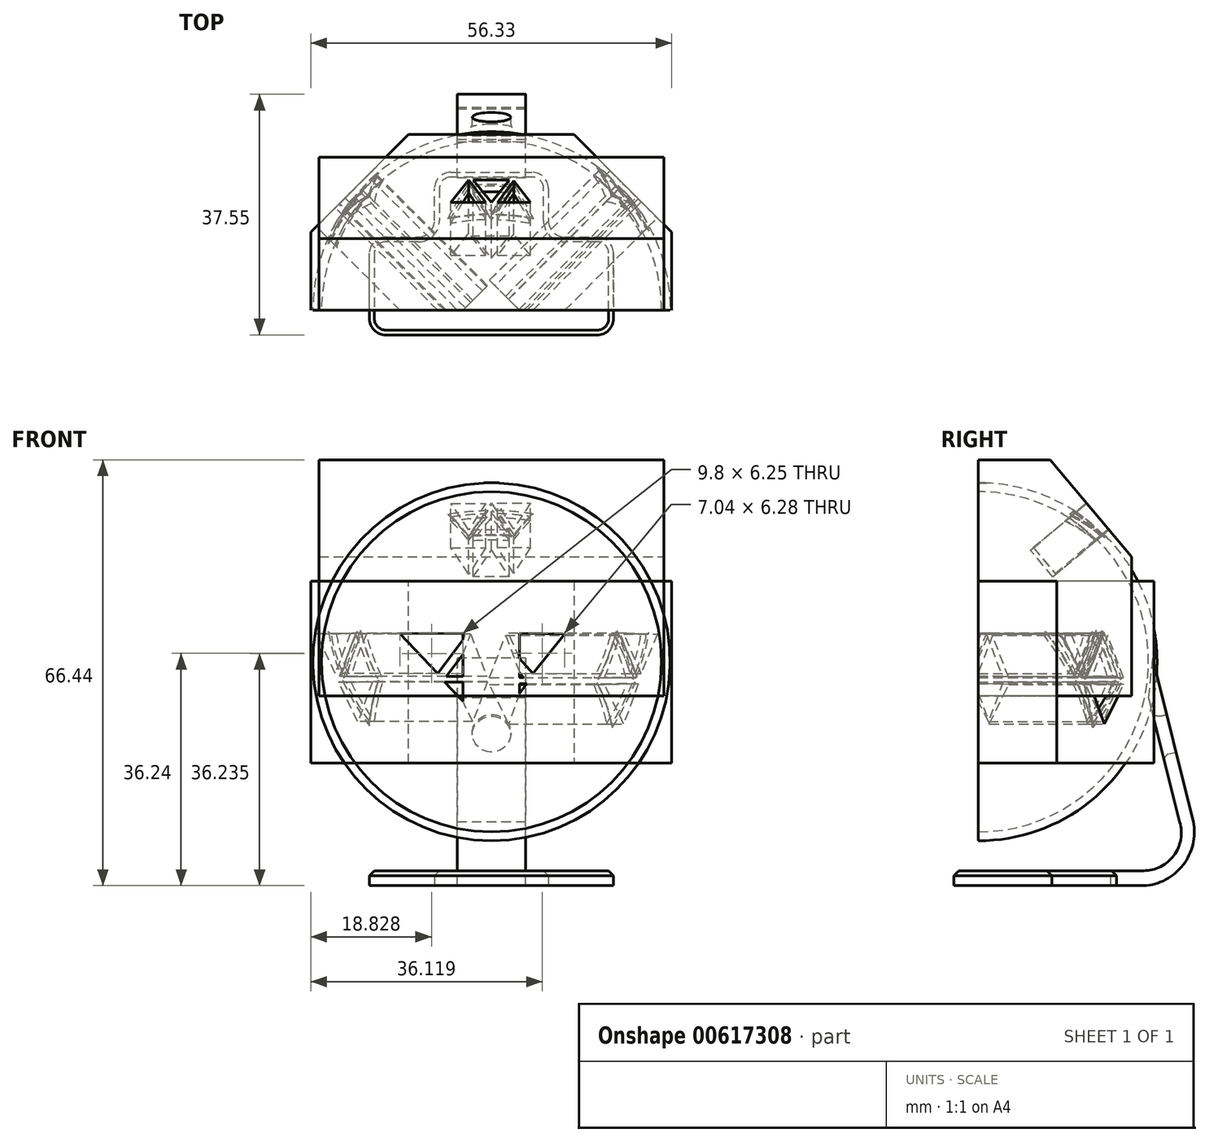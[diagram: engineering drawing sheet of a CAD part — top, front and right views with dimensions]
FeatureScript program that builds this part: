
annotation { "Feature Type Name" : "Feature", "Feature Type Description" : "" }
export const myFeature = defineFeature(function(context is Context, id is Id, definition is map)
    precondition{}
    {
        {
            var Q0;
            Q0=qCreatedBy(makeId("Front.planeOp"),FACE);
            var sketch = newSketch(context, id + "F0", { "sketchPlane" : qUnion([Q0])});
            skLineSegment(sketch, "E0", {"start": v(0, 76.83) * mm, "end": v(0, 0) * mm, "construction": true});
            skCircle(sketch, "E1", {"center": v(0, 34.92) * mm, "radius": 26.54 * mm});
            skCircle(sketch, "E2", {"center": v(0, 34.92) * mm, "radius": 27.94 * mm});
            skSolve(sketch);
        }
        {
            var Q0;
            Q0=makeQuery(id+"F0.imprint","IMPRINT",FACE,{"disambiguationData":[TD([[makeQuery(id+"F0.imprint","IMPRINT",EDGE,{"derivedFrom":sQuery(id+"F0.wireOp",EDGE,"E1")}),-1.0]])]});
            var sketch = newSketch(context, id + "F1", { "sketchPlane" : qUnion([Q0])});
            skArc(sketch, "E3", {"start": v(0, 6.99) * mm, "mid": v(27.88, 34.93) * mm, "end": v(0, 62.87) * mm});
            skLineSegment(sketch, "E4", {"start": v(0, 65.66) * mm, "end": v(0, 3.57) * mm});
            skSolve(sketch);
        }
        {
            var Q0;
            Q0=makeQuery(id+"F0.imprint","IMPRINT",FACE,{"disambiguationData":[TD([[makeQuery(id+"F0.imprint","IMPRINT",EDGE,{"derivedFrom":sQuery(id+"F0.wireOp",EDGE,"E1")}),1.0]])]});
            var sketch = newSketch(context, id + "F2", { "sketchPlane" : qUnion([Q0])});
            skArc(sketch, "E5", {"start": v(0, 61.48) * mm, "mid": v(-26.45, 34.93) * mm, "end": v(0, 8.38) * mm});
            skSolve(sketch);
        }
        {
            var Q0;
            Q0=sQuery(id+"F2.wireOp",EDGE,"E5");
            var Q1;
            Q1=sQuery(id+"F0.wireOp",EDGE,"E0");
            revolve(context, id + "F3", {"bodyType" : ToolBodyType.SURFACE, "surfaceEntities" : qUnion([Q0]), "axis" : qUnion([Q1]), "revolveType" : RevolveType.ONE_DIRECTION, "angle" : 180 * degree});
        }
        {
            var Q0;
            {var subQ0=sQuery(id+"F1.wireOp",EDGE,"E3");var subQ3=sQuery(id+"F1.wireOp",EDGE,"E4");var subQ7=makeQuery(id+"F1.imprint","INTERSECT",VERTEX,{"disambiguationData":[OD(0.0)],"derivedFrom":[subQ0,subQ3]});Q0=makeQuery(id+"F1.imprint","IMPRINT",FACE,{"disambiguationData":[TD([[makeQuery(id+"F1.imprint","IMPRINT",EDGE,{"disambiguationData":[TD([[subQ7,-1.0]])],"derivedFrom":subQ0}),1.0]])]});}
            var Q1;
            Q1=sQuery(id+"F1.wireOp",EDGE,"E4");
            revolve(context, id + "F4", {"entities" : qUnion([Q0]), "axis" : qUnion([Q1]), "revolveType" : RevolveType.ONE_DIRECTION, "oppositeDirection" : true, "angle" : 180 * degree});
        }
        {
            var Q0;
            Q0=qCreatedBy(makeId("Top.planeOp"),FACE);
            var sketch = newSketch(context, id + "F5", { "sketchPlane" : qUnion([Q0])});
            skLineSegment(sketch, "E6.bottom", {"start": v(0, -3.84) * mm, "end": v(19.05, -3.84) * mm});
            skLineSegment(sketch, "E6.top", {"start": v(0, 21.56) * mm, "end": v(19.05, 21.56) * mm});
            skLineSegment(sketch, "E6.left", {"start": v(0, -3.84) * mm, "end": v(0, 21.56) * mm});
            skLineSegment(sketch, "E6.right", {"start": v(19.05, -3.84) * mm, "end": v(19.05, 21.56) * mm});
            skLineSegment(sketch, "E7.bottom", {"start": v(0, -3.84) * mm, "end": v(-19.05, -3.84) * mm});
            skLineSegment(sketch, "E7.top", {"start": v(0, 21.56) * mm, "end": v(-19.05, 21.56) * mm});
            skLineSegment(sketch, "E7.right", {"start": v(-19.05, -3.84) * mm, "end": v(-19.05, 21.56) * mm});
            skLineSegment(sketch, "E8", {"start": v(-19.05, 11.45) * mm, "end": v(-8.9, 11.45) * mm});
            skLineSegment(sketch, "E9", {"start": v(8.89, 11.45) * mm, "end": v(19.05, 11.45) * mm});
            skLineSegment(sketch, "E10", {"start": v(-8.9, 11.45) * mm, "end": v(-8.9, 21.56) * mm});
            skLineSegment(sketch, "E11", {"start": v(8.89, 11.45) * mm, "end": v(8.89, 21.56) * mm});
            skSolve(sketch);
        }
        {
            var Q0;
            {var subQ2=sQuery(id+"F5.wireOp",EDGE,"E6.bottom");Q0=makeQuery(id+"F5.imprint","IMPRINT",FACE,{"disambiguationData":[TD([[makeQuery(id+"F5.imprint","IMPRINT",EDGE,{"derivedFrom":subQ2}),1.0]])]});}
            var Q1;
            {var subQ1=sQuery(id+"F5.wireOp",EDGE,"E7.bottom");Q1=makeQuery(id+"F5.imprint","IMPRINT",FACE,{"disambiguationData":[TD([[makeQuery(id+"F5.imprint","IMPRINT",EDGE,{"derivedFrom":subQ1}),-1.0]])]});}
            extrude(context, id + "F6", {"entities" : qUnion([Q0, Q1]), "depth" : 2.3 * mm, "offsetDistance" : 25.4 * mm});
        }
        {
            var Q0;
            Q0=qCreatedBy(makeId("Right.planeOp"),FACE);
            var sketch = newSketch(context, id + "F7", { "sketchPlane" : qUnion([Q0])});
            skLineSegment(sketch, "E12", {"start": v(27.23, 35.5) * mm, "end": v(33.46, 10.43) * mm});
            skLineSegment(sketch, "E13", {"start": v(20.68, 0) * mm, "end": v(26.25, 0) * mm});
            skArc(sketch, "E14", {"start": v(26.25, 0) * mm, "mid": v(32.21, 3.59) * mm, "end": v(33.46, 10.43) * mm});
            skLineSegment(sketch, "E15", {"start": v(20.68, 0) * mm, "end": v(20.68, 2.33) * mm});
            skLineSegment(sketch, "E16", {"start": v(20.68, 2.33) * mm, "end": v(25.8, 2.33) * mm});
            skLineSegment(sketch, "E17", {"start": v(33.46, 10.43) * mm, "end": v(31.42, 9.92) * mm});
            skLineSegment(sketch, "E18", {"start": v(31.42, 9.92) * mm, "end": v(26.6, 29.29) * mm});
            skLineSegment(sketch, "E19", {"start": v(26.6, 29.29) * mm, "end": v(27.23, 35.5) * mm});
            skArc(sketch, "E20", {"start": v(25.8, 2.33) * mm, "mid": v(30.52, 4.7) * mm, "end": v(31.42, 9.92) * mm});
            skSolve(sketch);
        }
        {
            var Q0;
            Q0=makeQuery(id+"F6.opExtrude","SWEPT_EDGE",EDGE,{"disambiguationData":[OSD([sQuery(id+"F5.wireOp",EDGE,"E7.bottom"),sQuery(id+"F5.wireOp",EDGE,"E7.right")])]});
            var Q1;
            Q1=makeQuery(id+"F6.opExtrude","SWEPT_EDGE",EDGE,{"disambiguationData":[OSD([sQuery(id+"F5.wireOp",EDGE,"E7.right"),sQuery(id+"F5.wireOp",EDGE,"E8")])]});
            var Q2;
            Q2=makeQuery(id+"F6.opExtrude","SWEPT_EDGE",EDGE,{"disambiguationData":[OSD([sQuery(id+"F5.wireOp",EDGE,"E7.top"),sQuery(id+"F5.wireOp",EDGE,"E10")])]});
            var Q3;
            Q3=makeQuery(id+"F6.opExtrude","SWEPT_EDGE",EDGE,{"disambiguationData":[OSD([sQuery(id+"F5.wireOp",EDGE,"E6.bottom"),sQuery(id+"F5.wireOp",EDGE,"E6.right")])]});
            var Q4;
            Q4=makeQuery(id+"F6.opExtrude","SWEPT_EDGE",EDGE,{"disambiguationData":[OSD([sQuery(id+"F5.wireOp",EDGE,"E6.right"),sQuery(id+"F5.wireOp",EDGE,"E9")])]});
            var Q5;
            Q5=makeQuery(id+"F6.opExtrude","SWEPT_EDGE",EDGE,{"disambiguationData":[OSD([sQuery(id+"F5.wireOp",EDGE,"E6.top"),sQuery(id+"F5.wireOp",EDGE,"E11")])]});
            var Q6;
            Q6=makeQuery(id+"F6.opExtrude","SWEPT_EDGE",EDGE,{"disambiguationData":[OSD([sQuery(id+"F5.wireOp",EDGE,"E8"),sQuery(id+"F5.wireOp",EDGE,"E10")])]});
            var Q7;
            Q7=makeQuery(id+"F6.opExtrude","SWEPT_EDGE",EDGE,{"disambiguationData":[OSD([sQuery(id+"F5.wireOp",EDGE,"E9"),sQuery(id+"F5.wireOp",EDGE,"E11")])]});
            fillet(context, id + "F8", {"entities" : qUnion([Q0, Q1, Q2, Q3, Q4, Q5, Q6, Q7]), "radius" : 2.54 * mm, "tangentPropagation" : true, "allowEdgeOverflow" : false});
        }
        {
            var Q0;
            Q0=makeQuery(id+"F7.imprint","IMPRINT",FACE,{"disambiguationData":[TD([[makeQuery(id+"F7.imprint","IMPRINT",EDGE,{"derivedFrom":sQuery(id+"F7.wireOp",EDGE,"E13")}),1.0]])]});
            var Q1;
            Q1=makeQuery(id+"F7.imprint","IMPRINT",FACE,{"disambiguationData":[TD([[makeQuery(id+"F7.imprint","IMPRINT",EDGE,{"derivedFrom":sQuery(id+"F7.wireOp",EDGE,"E12")}),-1.0]])]});
            extrude(context, id + "F9", {"entities" : qUnion([Q0, Q1]), "endBound" : BoundingType.SYMMETRIC, "depth" : 10.67 * mm, "offsetDistance" : 25.4 * mm});
        }
        {
            var Q0;
            Q0=makeQuery(id+"F6.opExtrude","CAP_EDGE",EDGE,{"disambiguationData":[OSD([sQuery(id+"F5.wireOp",EDGE,"E6.bottom"),sQuery(id+"F5.wireOp",EDGE,"E7.bottom")])],"isStart":false});
            var Q1;
            {var subQ0=sQuery(id+"F5.wireOp",EDGE,"E7.right");var subQ1=sQuery(id+"F5.wireOp",EDGE,"E7.bottom");Q1=makeQuery(id+"F8.opFillet","BLEND_EDGE",EDGE,{"blendedFrom":[makeQuery(id+"F6.opExtrude","SWEPT_EDGE",EDGE,{"disambiguationData":[OSD([subQ1,subQ0])]}),makeQuery(id+"F6.opExtrude","CAP_FACE",FACE,{"disambiguationData":[OSD([sQuery(id+"F5.wireOp",EDGE,"E6.bottom"),sQuery(id+"F5.wireOp",EDGE,"E6.top"),sQuery(id+"F5.wireOp",EDGE,"E6.right"),subQ1,sQuery(id+"F5.wireOp",EDGE,"E7.top"),subQ0,sQuery(id+"F5.wireOp",EDGE,"E8"),sQuery(id+"F5.wireOp",EDGE,"E9"),sQuery(id+"F5.wireOp",EDGE,"E10"),sQuery(id+"F5.wireOp",EDGE,"E11")])],"isStart":false})],"blendedInto":[makeQuery(id+"F6.opExtrude","CAP_FACE",FACE,{"disambiguationData":[OSD([sQuery(id+"F5.wireOp",EDGE,"E6.bottom"),sQuery(id+"F5.wireOp",EDGE,"E6.top"),sQuery(id+"F5.wireOp",EDGE,"E6.right"),subQ1,sQuery(id+"F5.wireOp",EDGE,"E7.top"),subQ0,sQuery(id+"F5.wireOp",EDGE,"E8"),sQuery(id+"F5.wireOp",EDGE,"E9"),sQuery(id+"F5.wireOp",EDGE,"E10"),sQuery(id+"F5.wireOp",EDGE,"E11")])],"isStart":false})]});}
            var Q2;
            Q2=makeQuery(id+"F6.opExtrude","CAP_EDGE",EDGE,{"disambiguationData":[OSD([sQuery(id+"F5.wireOp",EDGE,"E7.right")])],"isStart":false});
            var Q3;
            {var subQ0=sQuery(id+"F5.wireOp",EDGE,"E8");var subQ1=sQuery(id+"F5.wireOp",EDGE,"E7.right");Q3=makeQuery(id+"F8.opFillet","BLEND_EDGE",EDGE,{"blendedFrom":[makeQuery(id+"F6.opExtrude","SWEPT_EDGE",EDGE,{"disambiguationData":[OSD([subQ1,subQ0])]}),makeQuery(id+"F6.opExtrude","CAP_FACE",FACE,{"disambiguationData":[OSD([sQuery(id+"F5.wireOp",EDGE,"E6.bottom"),sQuery(id+"F5.wireOp",EDGE,"E6.top"),sQuery(id+"F5.wireOp",EDGE,"E6.right"),sQuery(id+"F5.wireOp",EDGE,"E7.bottom"),sQuery(id+"F5.wireOp",EDGE,"E7.top"),subQ1,subQ0,sQuery(id+"F5.wireOp",EDGE,"E9"),sQuery(id+"F5.wireOp",EDGE,"E10"),sQuery(id+"F5.wireOp",EDGE,"E11")])],"isStart":false})],"blendedInto":[makeQuery(id+"F6.opExtrude","CAP_FACE",FACE,{"disambiguationData":[OSD([sQuery(id+"F5.wireOp",EDGE,"E6.bottom"),sQuery(id+"F5.wireOp",EDGE,"E6.top"),sQuery(id+"F5.wireOp",EDGE,"E6.right"),sQuery(id+"F5.wireOp",EDGE,"E7.bottom"),sQuery(id+"F5.wireOp",EDGE,"E7.top"),subQ1,subQ0,sQuery(id+"F5.wireOp",EDGE,"E9"),sQuery(id+"F5.wireOp",EDGE,"E10"),sQuery(id+"F5.wireOp",EDGE,"E11")])],"isStart":false})]});}
            var Q4;
            Q4=makeQuery(id+"F6.opExtrude","CAP_EDGE",EDGE,{"disambiguationData":[OSD([sQuery(id+"F5.wireOp",EDGE,"E8")])],"isStart":false});
            var Q5;
            Q5=makeQuery(id+"F6.opExtrude","CAP_FACE",FACE,{"disambiguationData":[OSD([sQuery(id+"F5.wireOp",EDGE,"E6.bottom"),sQuery(id+"F5.wireOp",EDGE,"E6.top"),sQuery(id+"F5.wireOp",EDGE,"E6.right"),sQuery(id+"F5.wireOp",EDGE,"E7.bottom"),sQuery(id+"F5.wireOp",EDGE,"E7.top"),sQuery(id+"F5.wireOp",EDGE,"E7.right"),sQuery(id+"F5.wireOp",EDGE,"E8"),sQuery(id+"F5.wireOp",EDGE,"E9"),sQuery(id+"F5.wireOp",EDGE,"E10"),sQuery(id+"F5.wireOp",EDGE,"E11")])],"isStart":false});
            chamfer(context, id + "F10", {"entities" : qUnion([Q0, Q1, Q2, Q3, Q4, Q5]), "width" : 0.76 * mm, "tangentPropagation" : true});
        }
        {
            var Q0;
            Q0=makeQuery(id+"F9.opExtrude","SWEPT_FACE",FACE,{"disambiguationData":[OSD([sQuery(id+"F7.wireOp",EDGE,"E12")])]});
            var sketch = newSketch(context, id + "F11", { "sketchPlane" : qUnion([Q0])});
            skLineSegment(sketch, "E21", {"start": v(-5.33, 15.8) * mm, "end": v(5.33, 15.8) * mm, "construction": true});
            skCircle(sketch, "E22", {"center": v(0, 15.8) * mm, "radius": 3.01 * mm});
            skSolve(sketch);
        }
        {
            var Q0;
            Q0=makeQuery(id+"F11.imprint","IMPRINT",FACE,{"disambiguationData":[TD([[makeQuery(id+"F11.imprint","IMPRINT",EDGE,{"derivedFrom":sQuery(id+"F11.wireOp",EDGE,"E22")}),1.0]])]});
            extrude(context, id + "F12", {"entities" : qUnion([Q0]), "operationType" : NewBodyOperationType.REMOVE, "oppositeDirection" : true, "depth" : 2.92 * mm, "offsetDistance" : 25.4 * mm});
        }
        {
            var Q0;
            Q0=makeQuery(id+"F12.boolean.opBoolean","COPY",EDGE,{"derivedFrom":makeQuery(id+"F12.opExtrude","CAP_EDGE",EDGE,{"disambiguationData":[OSD([sQuery(id+"F11.wireOp",EDGE,"E22")])],"isStart":true})});
            var Q1;
            Q1=makeQuery(id+"F12.boolean.opBoolean","INTERSECT",EDGE,{"derivedFrom":[makeQuery(id+"F9.opExtrude","SWEPT_FACE",FACE,{"disambiguationData":[OSD([sQuery(id+"F7.wireOp",EDGE,"E18")])]}),makeQuery(id+"F12.opExtrude","SWEPT_FACE",FACE,{"disambiguationData":[OSD([sQuery(id+"F11.wireOp",EDGE,"E22")])]})]});
            fillet(context, id + "F13", {"entities" : qUnion([Q0, Q1]), "radius" : 1.04 * mm, "tangentPropagation" : true, "allowEdgeOverflow" : false});
        }
        {
            var Q0;
            Q0=qCreatedBy(makeId("Front.planeOp"),FACE);
            var sketch = newSketch(context, id + "F14", { "sketchPlane" : qUnion([Q0])});
            skLineSegment(sketch, "E23.bottom", {"start": v(26.92, 66.44) * mm, "end": v(-26.92, 66.44) * mm});
            skLineSegment(sketch, "E23.top", {"start": v(26.92, 29.63) * mm, "end": v(-26.92, 29.63) * mm});
            skLineSegment(sketch, "E23.left", {"start": v(26.92, 66.44) * mm, "end": v(26.92, 29.63) * mm});
            skLineSegment(sketch, "E23.right", {"start": v(-26.92, 66.44) * mm, "end": v(-26.92, 29.63) * mm});
            skSolve(sketch);
        }
        {
            var Q0;
            Q0 = qSketchRegion(id + "F14", true);
            extrude(context, id + "F15", {"entities" : qUnion([Q0]), "oppositeDirection" : true, "depth" : 23.88 * mm, "offsetDistance" : 25.4 * mm});
        }
        {
            var Q0;
            Q0=makeQuery(id+"F15.opExtrude","CAP_EDGE",EDGE,{"disambiguationData":[OSD([sQuery(id+"F14.wireOp",EDGE,"E23.bottom")])],"isStart":false});
            chamfer(context, id + "F16", {"entities" : qUnion([Q0]), "chamferType" : ChamferType.OFFSET_ANGLE, "width" : 12.7 * mm, "oppositeDirection" : false, "angle" : 50 * degree, "tangentPropagation" : true});
        }
        {
            var Q0;
            Q0=makeQuery(id+"F16.opChamfer","BLEND_FACE",FACE,{"disambiguationData":[OSD([sQuery(id+"F14.wireOp",EDGE,"E23.bottom")])]});
            var sketch = newSketch(context, id + "F17", { "sketchPlane" : qUnion([Q0])});
            skLineSegment(sketch, "E24", {"start": v(0, 34.88) * mm, "end": v(-2.76, 29.45) * mm});
            skLineSegment(sketch, "E25", {"start": v(-2.76, 29.45) * mm, "end": v(2.86, 29.45) * mm});
            skLineSegment(sketch, "E26", {"start": v(2.86, 29.45) * mm, "end": v(0, 34.88) * mm});
            skLineSegment(sketch, "E27", {"start": v(-3.45, 29.63) * mm, "end": v(-0.93, 34.91) * mm});
            skLineSegment(sketch, "E28", {"start": v(-0.93, 34.91) * mm, "end": v(-6.06, 34.91) * mm});
            skLineSegment(sketch, "E29", {"start": v(-6.06, 34.91) * mm, "end": v(-3.45, 29.63) * mm});
            skLineSegment(sketch, "E30", {"start": v(3.55, 29.48) * mm, "end": v(6.35, 34.86) * mm});
            skLineSegment(sketch, "E31", {"start": v(6.35, 34.86) * mm, "end": v(0.9, 34.86) * mm});
            skLineSegment(sketch, "E32", {"start": v(0.9, 34.86) * mm, "end": v(3.55, 29.48) * mm});
            skSolve(sketch);
        }
        {
            var Q0;
            Q0=makeQuery(id+"F17.imprint","IMPRINT",FACE,{"disambiguationData":[TD([[makeQuery(id+"F17.imprint","IMPRINT",EDGE,{"derivedFrom":sQuery(id+"F17.wireOp",EDGE,"E24")}),1.0]])]});
            var Q1;
            Q1=makeQuery(id+"F4.opRevolve","SWEPT_BODY",BODY,{"disambiguationData":[OSD([sQuery(id+"F0.wireOp",EDGE,"E1"),sQuery(id+"F0.wireOp",EDGE,"E2"),sQuery(id+"F1.wireOp",EDGE,"E3"),sQuery(id+"F1.wireOp",EDGE,"E4")])]});
            extrude(context, id + "F18", {"entities" : qUnion([Q0]), "operationType" : NewBodyOperationType.REMOVE, "oppositeDirection" : true, "depth" : 11.4 * mm, "endBoundEntityBody" : qUnion([Q1]), "offsetDistance" : 25.4 * mm});
        }
        {
            var Q0;
            Q0=makeQuery(id+"F17.imprint","IMPRINT",FACE,{"disambiguationData":[TD([[makeQuery(id+"F17.imprint","IMPRINT",EDGE,{"derivedFrom":sQuery(id+"F17.wireOp",EDGE,"E27")}),1.0]])]});
            var Q1;
            Q1=makeQuery(id+"F17.imprint","IMPRINT",FACE,{"disambiguationData":[TD([[makeQuery(id+"F17.imprint","IMPRINT",EDGE,{"derivedFrom":sQuery(id+"F17.wireOp",EDGE,"E30")}),1.0]])]});
            extrude(context, id + "F19", {"entities" : qUnion([Q0, Q1]), "operationType" : NewBodyOperationType.REMOVE, "oppositeDirection" : true, "depth" : 10.8 * mm, "offsetDistance" : 25.4 * mm});
        }
        {
            var Q0;
            Q0=qCreatedBy(makeId("Front.planeOp"),FACE);
            var sketch = newSketch(context, id + "F20", { "sketchPlane" : qUnion([Q0])});
            skLineSegment(sketch, "E33.bottom", {"start": v(28.13, 47.53) * mm, "end": v(-28.2, 47.53) * mm});
            skLineSegment(sketch, "E33.top", {"start": v(28.13, 19.1) * mm, "end": v(-28.2, 19.1) * mm});
            skLineSegment(sketch, "E33.left", {"start": v(28.13, 47.53) * mm, "end": v(28.13, 19.1) * mm});
            skLineSegment(sketch, "E33.right", {"start": v(-28.2, 47.53) * mm, "end": v(-28.2, 19.1) * mm});
            skSolve(sketch);
        }
        {
            var Q0;
            Q0=makeQuery(id+"F20.imprint","IMPRINT",FACE,{"disambiguationData":[TD([[makeQuery(id+"F20.imprint","IMPRINT",EDGE,{"derivedFrom":sQuery(id+"F20.wireOp",EDGE,"E33.bottom")}),1.0]])]});
            extrude(context, id + "F21", {"entities" : qUnion([Q0]), "oppositeDirection" : true, "depth" : 27.43 * mm, "offsetDistance" : 25.4 * mm});
        }
        {
            var Q0;
            Q0=makeQuery(id+"F21.opExtrude","CAP_EDGE",EDGE,{"disambiguationData":[OSD([sQuery(id+"F20.wireOp",EDGE,"E33.left")])],"isStart":false});
            var Q1;
            Q1=makeQuery(id+"F21.opExtrude","CAP_EDGE",EDGE,{"disambiguationData":[OSD([sQuery(id+"F20.wireOp",EDGE,"E33.right")])],"isStart":false});
            chamfer(context, id + "F22", {"entities" : qUnion([Q0, Q1]), "chamferType" : ChamferType.OFFSET_ANGLE, "width" : 15.24 * mm, "oppositeDirection" : false, "angle" : 45 * degree, "tangentPropagation" : true});
        }
        {
            var Q0;
            Q0=makeQuery(id+"F22.opChamfer","BLEND_FACE",FACE,{"disambiguationData":[OSD([sQuery(id+"F20.wireOp",EDGE,"E33.left")])]});
            var sketch = newSketch(context, id + "F23", { "sketchPlane" : qUnion([Q0])});
            skLineSegment(sketch, "E34", {"start": v(0, 39.04) * mm, "end": v(-3.54, 32.45) * mm});
            skLineSegment(sketch, "E35", {"start": v(-3.54, 32.45) * mm, "end": v(3.54, 32.45) * mm});
            skLineSegment(sketch, "E36", {"start": v(3.54, 32.45) * mm, "end": v(0, 39.04) * mm});
            skLineSegment(sketch, "E37", {"start": v(-0.62, 39.46) * mm, "end": v(-8.09, 39.23) * mm});
            skLineSegment(sketch, "E38", {"start": v(-8.09, 39.23) * mm, "end": v(-4.55, 33.1) * mm});
            skLineSegment(sketch, "E39", {"start": v(-4.55, 33.1) * mm, "end": v(-0.62, 39.46) * mm});
            skLineSegment(sketch, "E40", {"start": v(3.56, 31.4) * mm, "end": v(-3.91, 31.54) * mm});
            skLineSegment(sketch, "E41", {"start": v(-3.91, 31.54) * mm, "end": v(-0.69, 25.24) * mm});
            skLineSegment(sketch, "E42", {"start": v(-0.69, 25.24) * mm, "end": v(3.56, 31.4) * mm});
            skSolve(sketch);
        }
        {
            var Q0;
            Q0=makeQuery(id+"F23.imprint","IMPRINT",FACE,{"disambiguationData":[TD([[makeQuery(id+"F23.imprint","IMPRINT",EDGE,{"derivedFrom":sQuery(id+"F23.wireOp",EDGE,"E34")}),1.0]])]});
            extrude(context, id + "F24", {"entities" : qUnion([Q0]), "operationType" : NewBodyOperationType.REMOVE, "oppositeDirection" : true, "depth" : 25.4 * mm, "offsetDistance" : 25.4 * mm});
        }
        {
            var Q0;
            Q0=makeQuery(id+"F23.imprint","IMPRINT",FACE,{"disambiguationData":[TD([[makeQuery(id+"F23.imprint","IMPRINT",EDGE,{"derivedFrom":sQuery(id+"F23.wireOp",EDGE,"E37")}),1.0]])]});
            var Q1;
            Q1=makeQuery(id+"F23.imprint","IMPRINT",FACE,{"disambiguationData":[TD([[makeQuery(id+"F23.imprint","IMPRINT",EDGE,{"derivedFrom":sQuery(id+"F23.wireOp",EDGE,"E40")}),1.0]])]});
            extrude(context, id + "F25", {"entities" : qUnion([Q0, Q1]), "operationType" : NewBodyOperationType.REMOVE, "oppositeDirection" : true, "depth" : 25.4 * mm, "offsetDistance" : 25.4 * mm});
        }
        {
            var Q0;
            Q0=makeQuery(id+"F22.opChamfer","BLEND_FACE",FACE,{"disambiguationData":[OSD([sQuery(id+"F20.wireOp",EDGE,"E33.right")])]});
            var sketch = newSketch(context, id + "F26", { "sketchPlane" : qUnion([Q0])});
            skLineSegment(sketch, "E43", {"start": v(1.44, 39.26) * mm, "end": v(-2.1, 32.67) * mm});
            skLineSegment(sketch, "E44", {"start": v(-2.1, 32.67) * mm, "end": v(4.98, 32.67) * mm});
            skLineSegment(sketch, "E45", {"start": v(4.98, 32.67) * mm, "end": v(1.44, 39.26) * mm});
            skPoint(sketch, "E46.centerSnap0", {"position": v(1.44, 32.67) * mm});
            skLineSegment(sketch, "E47", {"start": v(10.1, 39.32) * mm, "end": v(2.62, 39.36) * mm});
            skLineSegment(sketch, "E48", {"start": v(2.62, 39.36) * mm, "end": v(5.93, 33.11) * mm});
            skLineSegment(sketch, "E49", {"start": v(5.93, 33.11) * mm, "end": v(10.1, 39.32) * mm});
            skPoint(sketch, "E50.centerSnap0", {"position": v(4.27, 36.24) * mm});
            skLineSegment(sketch, "E51.0", {"start": v(4.27, 36.24) * mm, "end": v(6.85, 37.6) * mm, "construction": true});
            skLineSegment(sketch, "E52", {"start": v(5.19, 31.74) * mm, "end": v(-2.29, 31.85) * mm});
            skLineSegment(sketch, "E53", {"start": v(-2.29, 31.85) * mm, "end": v(0.96, 25.57) * mm});
            skLineSegment(sketch, "E54", {"start": v(0.96, 25.57) * mm, "end": v(5.19, 31.74) * mm});
            skPoint(sketch, "E55.centerSnap0", {"position": v(-0.66, 28.7) * mm});
            skLineSegment(sketch, "E56.0", {"start": v(-0.66, 28.7) * mm, "end": v(1.93, 30.05) * mm, "construction": true});
            skSolve(sketch);
        }
        {
            var Q0;
            Q0=makeQuery(id+"F26.imprint","IMPRINT",FACE,{"disambiguationData":[TD([[makeQuery(id+"F26.imprint","IMPRINT",EDGE,{"derivedFrom":sQuery(id+"F26.wireOp",EDGE,"E52")}),1.0]])]});
            var Q1;
            Q1=makeQuery(id+"F26.imprint","IMPRINT",FACE,{"disambiguationData":[TD([[makeQuery(id+"F26.imprint","IMPRINT",EDGE,{"derivedFrom":sQuery(id+"F26.wireOp",EDGE,"E43")}),1.0]])]});
            var Q2;
            Q2=makeQuery(id+"F26.imprint","IMPRINT",FACE,{"disambiguationData":[TD([[makeQuery(id+"F26.imprint","IMPRINT",EDGE,{"derivedFrom":sQuery(id+"F26.wireOp",EDGE,"E47")}),1.0]])]});
            extrude(context, id + "F27", {"entities" : qUnion([Q0, Q1, Q2]), "operationType" : NewBodyOperationType.REMOVE, "oppositeDirection" : true, "depth" : 25.4 * mm, "offsetDistance" : 25.4 * mm});
        }
        {
            var Q0;
            Q0=makeQuery(id+"F25.boolean.opBoolean","INTERSECT",EDGE,{"derivedFrom":[makeQuery(id+"F4.opRevolve","SWEPT_FACE",FACE,{"disambiguationData":[OSD([sQuery(id+"F1.wireOp",EDGE,"E3")])]}),makeQuery(id+"F25.opExtrude","SWEPT_FACE",FACE,{"disambiguationData":[OSD([sQuery(id+"F23.wireOp",EDGE,"E37")])]})]});
            var Q1;
            Q1=makeQuery(id+"F25.boolean.opBoolean","INTERSECT",EDGE,{"derivedFrom":[makeQuery(id+"F4.opRevolve","SWEPT_FACE",FACE,{"disambiguationData":[OSD([sQuery(id+"F1.wireOp",EDGE,"E3")])]}),makeQuery(id+"F25.opExtrude","SWEPT_FACE",FACE,{"disambiguationData":[OSD([sQuery(id+"F23.wireOp",EDGE,"E39")])]})]});
            var Q2;
            Q2=makeQuery(id+"F25.boolean.opBoolean","INTERSECT",EDGE,{"derivedFrom":[makeQuery(id+"F4.opRevolve","SWEPT_FACE",FACE,{"disambiguationData":[OSD([sQuery(id+"F1.wireOp",EDGE,"E3")])]}),makeQuery(id+"F25.opExtrude","SWEPT_FACE",FACE,{"disambiguationData":[OSD([sQuery(id+"F23.wireOp",EDGE,"E38")])]})]});
            var Q3;
            Q3=makeQuery(id+"F24.boolean.opBoolean","INTERSECT",EDGE,{"derivedFrom":[makeQuery(id+"F4.opRevolve","SWEPT_FACE",FACE,{"disambiguationData":[OSD([sQuery(id+"F1.wireOp",EDGE,"E3")])]}),makeQuery(id+"F24.opExtrude","SWEPT_FACE",FACE,{"disambiguationData":[OSD([sQuery(id+"F23.wireOp",EDGE,"E34")])]})]});
            var Q4;
            Q4=makeQuery(id+"F24.boolean.opBoolean","INTERSECT",EDGE,{"derivedFrom":[makeQuery(id+"F4.opRevolve","SWEPT_FACE",FACE,{"disambiguationData":[OSD([sQuery(id+"F1.wireOp",EDGE,"E3")])]}),makeQuery(id+"F24.opExtrude","SWEPT_FACE",FACE,{"disambiguationData":[OSD([sQuery(id+"F23.wireOp",EDGE,"E36")])]})]});
            var Q5;
            Q5=makeQuery(id+"F24.boolean.opBoolean","INTERSECT",EDGE,{"derivedFrom":[makeQuery(id+"F4.opRevolve","SWEPT_FACE",FACE,{"disambiguationData":[OSD([sQuery(id+"F1.wireOp",EDGE,"E3")])]}),makeQuery(id+"F24.opExtrude","SWEPT_FACE",FACE,{"disambiguationData":[OSD([sQuery(id+"F23.wireOp",EDGE,"E35")])]})]});
            var Q6;
            Q6=makeQuery(id+"F25.boolean.opBoolean","INTERSECT",EDGE,{"derivedFrom":[makeQuery(id+"F4.opRevolve","SWEPT_FACE",FACE,{"disambiguationData":[OSD([sQuery(id+"F1.wireOp",EDGE,"E3")])]}),makeQuery(id+"F25.opExtrude","SWEPT_FACE",FACE,{"disambiguationData":[OSD([sQuery(id+"F23.wireOp",EDGE,"E40")])]})]});
            var Q7;
            Q7=makeQuery(id+"F25.boolean.opBoolean","INTERSECT",EDGE,{"derivedFrom":[makeQuery(id+"F4.opRevolve","SWEPT_FACE",FACE,{"disambiguationData":[OSD([sQuery(id+"F1.wireOp",EDGE,"E3")])]}),makeQuery(id+"F25.opExtrude","SWEPT_FACE",FACE,{"disambiguationData":[OSD([sQuery(id+"F23.wireOp",EDGE,"E41")])]})]});
            var Q8;
            Q8=makeQuery(id+"F25.boolean.opBoolean","INTERSECT",EDGE,{"derivedFrom":[makeQuery(id+"F4.opRevolve","SWEPT_FACE",FACE,{"disambiguationData":[OSD([sQuery(id+"F1.wireOp",EDGE,"E3")])]}),makeQuery(id+"F25.opExtrude","SWEPT_FACE",FACE,{"disambiguationData":[OSD([sQuery(id+"F23.wireOp",EDGE,"E42")])]})]});
            var Q9;
            Q9=makeQuery(id+"F27.boolean.opBoolean","INTERSECT",EDGE,{"derivedFrom":[makeQuery(id+"F4.opRevolve","SWEPT_FACE",FACE,{"disambiguationData":[OSD([sQuery(id+"F1.wireOp",EDGE,"E3")])]}),makeQuery(id+"F27.opExtrude","SWEPT_FACE",FACE,{"disambiguationData":[OSD([sQuery(id+"F26.wireOp",EDGE,"E48")])]})]});
            var Q10;
            Q10=makeQuery(id+"F27.boolean.opBoolean","INTERSECT",EDGE,{"derivedFrom":[makeQuery(id+"F4.opRevolve","SWEPT_FACE",FACE,{"disambiguationData":[OSD([sQuery(id+"F1.wireOp",EDGE,"E3")])]}),makeQuery(id+"F27.opExtrude","SWEPT_FACE",FACE,{"disambiguationData":[OSD([sQuery(id+"F26.wireOp",EDGE,"E44")])]})]});
            var Q11;
            Q11=makeQuery(id+"F27.boolean.opBoolean","INTERSECT",EDGE,{"derivedFrom":[makeQuery(id+"F4.opRevolve","SWEPT_FACE",FACE,{"disambiguationData":[OSD([sQuery(id+"F1.wireOp",EDGE,"E3")])]}),makeQuery(id+"F27.opExtrude","SWEPT_FACE",FACE,{"disambiguationData":[OSD([sQuery(id+"F26.wireOp",EDGE,"E43")])]})]});
            var Q12;
            Q12=makeQuery(id+"F27.boolean.opBoolean","INTERSECT",EDGE,{"derivedFrom":[makeQuery(id+"F4.opRevolve","SWEPT_FACE",FACE,{"disambiguationData":[OSD([sQuery(id+"F1.wireOp",EDGE,"E3")])]}),makeQuery(id+"F27.opExtrude","SWEPT_FACE",FACE,{"disambiguationData":[OSD([sQuery(id+"F26.wireOp",EDGE,"E47")])]})]});
            var Q13;
            Q13=makeQuery(id+"F27.boolean.opBoolean","INTERSECT",EDGE,{"derivedFrom":[makeQuery(id+"F4.opRevolve","SWEPT_FACE",FACE,{"disambiguationData":[OSD([sQuery(id+"F1.wireOp",EDGE,"E3")])]}),makeQuery(id+"F27.opExtrude","SWEPT_FACE",FACE,{"disambiguationData":[OSD([sQuery(id+"F26.wireOp",EDGE,"E45")])]})]});
            var Q14;
            Q14=makeQuery(id+"F27.boolean.opBoolean","INTERSECT",EDGE,{"derivedFrom":[makeQuery(id+"F4.opRevolve","SWEPT_FACE",FACE,{"disambiguationData":[OSD([sQuery(id+"F1.wireOp",EDGE,"E3")])]}),makeQuery(id+"F27.opExtrude","SWEPT_FACE",FACE,{"disambiguationData":[OSD([sQuery(id+"F26.wireOp",EDGE,"E49")])]})]});
            var Q15;
            Q15=makeQuery(id+"F27.boolean.opBoolean","INTERSECT",EDGE,{"derivedFrom":[makeQuery(id+"F4.opRevolve","SWEPT_FACE",FACE,{"disambiguationData":[OSD([sQuery(id+"F1.wireOp",EDGE,"E3")])]}),makeQuery(id+"F27.opExtrude","SWEPT_FACE",FACE,{"disambiguationData":[OSD([sQuery(id+"F26.wireOp",EDGE,"E54")])]})]});
            var Q16;
            Q16=makeQuery(id+"F27.boolean.opBoolean","INTERSECT",EDGE,{"derivedFrom":[makeQuery(id+"F4.opRevolve","SWEPT_FACE",FACE,{"disambiguationData":[OSD([sQuery(id+"F1.wireOp",EDGE,"E3")])]}),makeQuery(id+"F27.opExtrude","SWEPT_FACE",FACE,{"disambiguationData":[OSD([sQuery(id+"F26.wireOp",EDGE,"E52")])]})]});
            var Q17;
            Q17=makeQuery(id+"F27.boolean.opBoolean","INTERSECT",EDGE,{"derivedFrom":[makeQuery(id+"F4.opRevolve","SWEPT_FACE",FACE,{"disambiguationData":[OSD([sQuery(id+"F1.wireOp",EDGE,"E3")])]}),makeQuery(id+"F27.opExtrude","SWEPT_FACE",FACE,{"disambiguationData":[OSD([sQuery(id+"F26.wireOp",EDGE,"E53")])]})]});
            var Q18;
            Q18=makeQuery(id+"F19.boolean.opBoolean","INTERSECT",EDGE,{"derivedFrom":[makeQuery(id+"F4.opRevolve","SWEPT_FACE",FACE,{"disambiguationData":[OSD([sQuery(id+"F1.wireOp",EDGE,"E3")])]}),makeQuery(id+"F19.opExtrude","SWEPT_FACE",FACE,{"disambiguationData":[OSD([sQuery(id+"F17.wireOp",EDGE,"E28")])]})]});
            var Q19;
            Q19=makeQuery(id+"F19.boolean.opBoolean","INTERSECT",EDGE,{"derivedFrom":[makeQuery(id+"F4.opRevolve","SWEPT_FACE",FACE,{"disambiguationData":[OSD([sQuery(id+"F1.wireOp",EDGE,"E3")])]}),makeQuery(id+"F19.opExtrude","SWEPT_FACE",FACE,{"disambiguationData":[OSD([sQuery(id+"F17.wireOp",EDGE,"E29")])]})]});
            var Q20;
            Q20=makeQuery(id+"F18.boolean.opBoolean","INTERSECT",EDGE,{"derivedFrom":[makeQuery(id+"F4.opRevolve","SWEPT_FACE",FACE,{"disambiguationData":[OSD([sQuery(id+"F1.wireOp",EDGE,"E3")])]}),makeQuery(id+"F18.opExtrude","SWEPT_FACE",FACE,{"disambiguationData":[OSD([sQuery(id+"F17.wireOp",EDGE,"E24")])]})]});
            var Q21;
            Q21=makeQuery(id+"F18.boolean.opBoolean","INTERSECT",EDGE,{"derivedFrom":[makeQuery(id+"F4.opRevolve","SWEPT_FACE",FACE,{"disambiguationData":[OSD([sQuery(id+"F1.wireOp",EDGE,"E3")])]}),makeQuery(id+"F18.opExtrude","SWEPT_FACE",FACE,{"disambiguationData":[OSD([sQuery(id+"F17.wireOp",EDGE,"E25")])]})]});
            var Q22;
            Q22=makeQuery(id+"F19.boolean.opBoolean","INTERSECT",EDGE,{"derivedFrom":[makeQuery(id+"F4.opRevolve","SWEPT_FACE",FACE,{"disambiguationData":[OSD([sQuery(id+"F1.wireOp",EDGE,"E3")])]}),makeQuery(id+"F19.opExtrude","SWEPT_FACE",FACE,{"disambiguationData":[OSD([sQuery(id+"F17.wireOp",EDGE,"E32")])]})]});
            var Q23;
            Q23=makeQuery(id+"F19.boolean.opBoolean","INTERSECT",EDGE,{"derivedFrom":[makeQuery(id+"F4.opRevolve","SWEPT_FACE",FACE,{"disambiguationData":[OSD([sQuery(id+"F1.wireOp",EDGE,"E3")])]}),makeQuery(id+"F19.opExtrude","SWEPT_FACE",FACE,{"disambiguationData":[OSD([sQuery(id+"F17.wireOp",EDGE,"E31")])]})]});
            var Q24;
            Q24=makeQuery(id+"F19.boolean.opBoolean","INTERSECT",EDGE,{"derivedFrom":[makeQuery(id+"F4.opRevolve","SWEPT_FACE",FACE,{"disambiguationData":[OSD([sQuery(id+"F1.wireOp",EDGE,"E3")])]}),makeQuery(id+"F19.opExtrude","SWEPT_FACE",FACE,{"disambiguationData":[OSD([sQuery(id+"F17.wireOp",EDGE,"E30")])]})]});
            fillet(context, id + "F28", {"entities" : qUnion([Q0, Q1, Q2, Q3, Q4, Q5, Q6, Q7, Q8, Q9, Q10, Q11, Q12, Q13, Q14, Q15, Q16, Q17, Q18, Q19, Q20, Q21, Q22, Q23, Q24]), "radius" : 0.25 * mm, "tangentPropagation" : true, "allowEdgeOverflow" : false});
        }
    });
